# Revit family: Lighting-ArredoUrbano-GEWISS-POINT-LED_ILLUMINAZIONE_GIARDINO
name_source: partatom
category: Apparecchi per illuminazione
units: mm (PartAtom-declared; Revit-internal decimal feet)

## family parameters
Condiviso = No
Host = Superficie
Numero OmniClass = 23.80.70.00
Punto di calcolo locali = Sì
Quota connettore circolare = Usa diametro
Sorgente d'illuminazione = No
Taglio con vuoti quando caricato = No
Tipo di parte = Normale
Titolo OmniClass = Lighting

## types (6) — shared parameters
2D LAT = 2D - POINT : 006
Altezza = 473 mm
Carico apparente = 4 VA
Catalogo = LIGHTING
Commenti sul wattaggio = 4W
Glow Wire Test = 650°C
IDF = a9958e68-dd21-43ca-9765-15268e6ed8c2
IDT = f2a9305b-c3d1-4dd3-b135-09b9879f617e
Immagine tipo = GW82006.jpg
Lampada = DR
Lampada: = DR
Numero di poli = 2
Numero lampade: = 1
Produttore = GEWISS S.p.A.
Prospetto di default = 1219 mm
Raggio = 69 mm
Raggio int = 45 mm  [stored 0.147638 ft]
SEO = Paletto
Scheda Tecnica = https://www.gewiss.com
Struttura = GEWISS - Grigio Grafite
Temperatura di colore = 3000K
Tensione = 230 V - 50 Hz
URL = https://www.gewiss.com
Versione file RFA = 20.11
Vetro = GEWISS - vetro acceso
Voltaggio = 230 V

## per-type parameters (varying)
| type | Altezza (mm) | Applicazione | Attacco lampada | Catalogo Serie | Classe di efficienza LED integrati | Classe isolamento | Codice EAN | Codice Electrocod | Colore | Descrizione | Garanzia | Grado di protezione | Inquinamento luminoso | Inquinamento luminoso: | Modello | Numero lampade | Potenza lampada | Resistenza agli urti | Temperatura di colore: | Tipologia sorgente luminosa |
| GW82011G - POINT PI.4W E14 DR 3000K GRIGIO GRAFITE | 473 | Esterno | E14 | POINT | D ÷ A+ | II | 8011564869004 | 2442 | Grigio grafite | POINT PICCOLO 4W E14 DR 3000K GRIGIO GRAFITE | Estendibile | IP55 | 25% | 25% | GW82011G | 1 | 4W | IK10 |  | A+ |
| GW82016B - POINT GR.11W E27 DR 3000K BLU | 550 | Esterno | E27 | POINT | D ÷ A+ | II | 8011564869035 | 2442 | Blu notte | POINT GRANDE 6W E27 DR 3000K BLU | Estendibile | IP55 | 25% | 25% | GW82016B | 1 | 6W | IK10 |  | A+ |
| GW82011B - POINT PI.4W E14 DR 3000K BLU | 473 | Esterno | E14 | POINT | D ÷ A+ | II | 8011564869028 | 2442 | Blu notte | POINT PICCOLO 4W E14 DR 3000K BLU | Estendibile | IP55 | 25% | 25% | GW82011B | 1 | 4W | IK10 |  | A+ |
| GW82018G - POINT 780MM 11W E27 DR 3000K GRIGIO | 780 |  | E27 |  |  |  |  | 2424 | Grigio grafite | POINT 780MM 11W E27 DR 3000K GRIGIO |  |  |  |  | GW82018G |  | 11W |  | 3000 K |  |
| GW82018B - POINT 780MM 11W E27 DR 3000K BLU | 780 |  | E27 |  |  |  |  | 2424 | BlueGreen | POINT 780MM 11W E27 DR 3000K BLU |  |  |  |  | GW82018B |  | 11W |  | 3000 K |  |
| GW82016G - POINT GR.11W E27 DR 3000K GRIGIO GRAFITE | 550 | Esterno | E27 | POINT | D ÷ A+ | II | 8011564869011 | 2442 | Grigio grafite | POINT GRANDE 6W E27 DR 3000K GRIGIO GRAFITE | Estendibile | IP55 | 25% | 25% | GW82016G | 1 | 6W | IK10 |  | A+ |

note: [stored X ft] marks values corroborated as IEEE doubles in the binary element streams (Revit-internal decimal feet)

## geometry (parser evidence)
native form markers: Blend x409
no freeform markers — native parametric forms only
